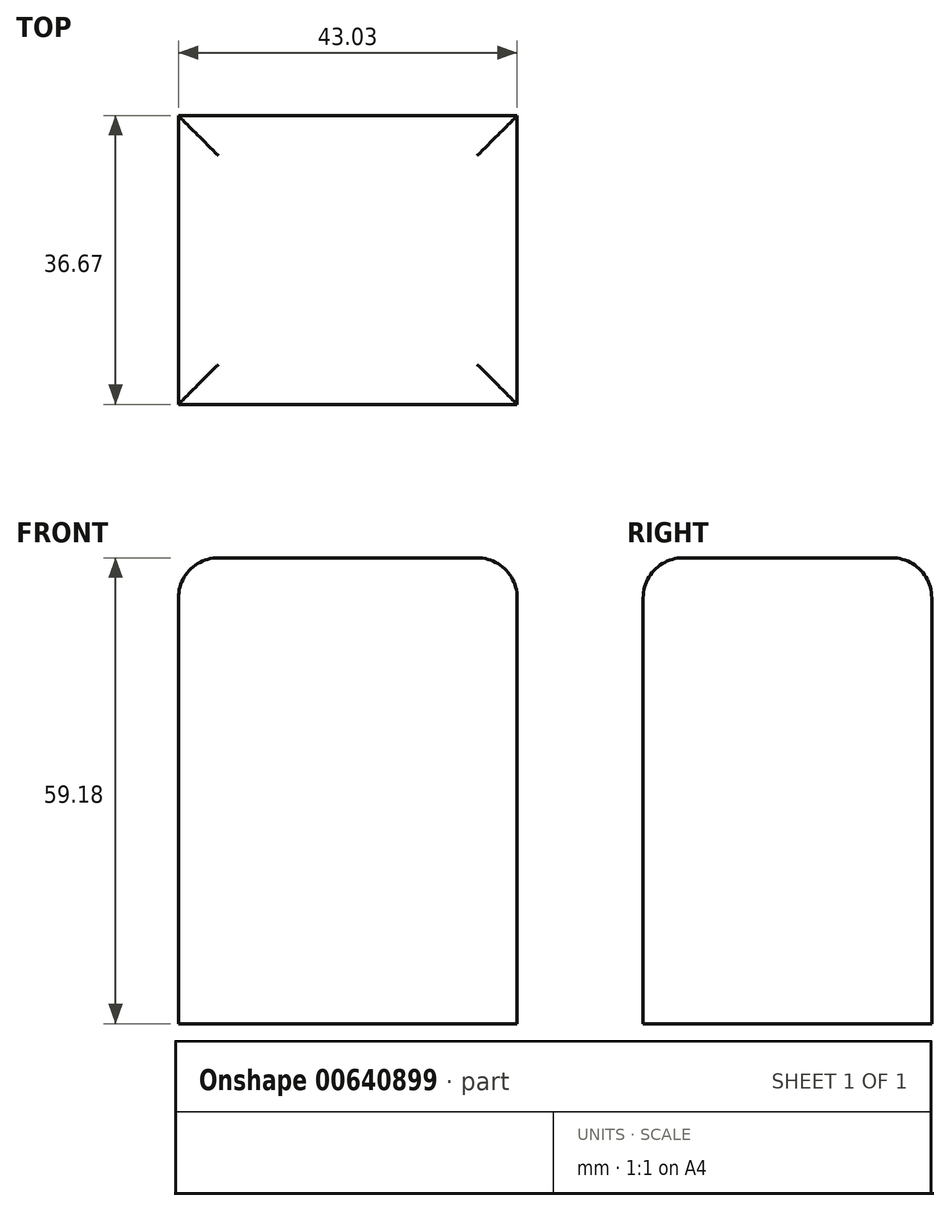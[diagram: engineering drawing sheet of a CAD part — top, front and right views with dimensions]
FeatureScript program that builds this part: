
annotation { "Feature Type Name" : "Feature", "Feature Type Description" : "" }
export const myFeature = defineFeature(function(context is Context, id is Id, definition is map)
    precondition{}
    {
        {
            var Q0;
            Q0=qCreatedBy(makeId("Top.planeOp"),FACE);
            var sketch = newSketch(context, id + "F0", { "sketchPlane" : qUnion([Q0])});
            skLineSegment(sketch, "E0.bottom", {"start": v(4.95, -29.68) * mm, "end": v(47.98, -29.68) * mm});
            skLineSegment(sketch, "E0.top", {"start": v(4.95, 6.99) * mm, "end": v(47.98, 6.99) * mm});
            skLineSegment(sketch, "E0.left", {"start": v(4.95, -29.68) * mm, "end": v(4.95, 6.99) * mm});
            skLineSegment(sketch, "E0.right", {"start": v(47.98, -29.68) * mm, "end": v(47.98, 6.99) * mm});
            skSolve(sketch);
        }
        {
            var Q0;
            Q0=makeQuery(id+"F0.imprint","IMPRINT",FACE,{"disambiguationData":[TD([[makeQuery(id+"F0.imprint","IMPRINT",EDGE,{"derivedFrom":sQuery(id+"F0.wireOp",EDGE,"E0.bottom")}),1.0]])]});
            extrude(context, id + "F1", {"entities" : qUnion([Q0]), "depth" : 59.18 * mm, "offsetDistance" : 25.4 * mm});
        }
        {
            var Q0;
            Q0=makeQuery(id+"F1.opExtrude","CAP_EDGE",EDGE,{"disambiguationData":[OSD([sQuery(id+"F0.wireOp",EDGE,"E0.bottom")])],"isStart":false});
            var Q1;
            Q1=makeQuery(id+"F1.opExtrude","CAP_EDGE",EDGE,{"disambiguationData":[OSD([sQuery(id+"F0.wireOp",EDGE,"E0.right")])],"isStart":false});
            var Q2;
            Q2=makeQuery(id+"F1.opExtrude","CAP_EDGE",EDGE,{"disambiguationData":[OSD([sQuery(id+"F0.wireOp",EDGE,"E0.top")])],"isStart":false});
            var Q3;
            Q3=makeQuery(id+"F1.opExtrude","CAP_EDGE",EDGE,{"disambiguationData":[OSD([sQuery(id+"F0.wireOp",EDGE,"E0.left")])],"isStart":false});
            fillet(context, id + "F2", {"entities" : qUnion([Q0, Q1, Q2, Q3]), "radius" : 5.08 * mm, "tangentPropagation" : true, "allowEdgeOverflow" : false});
        }
    });
